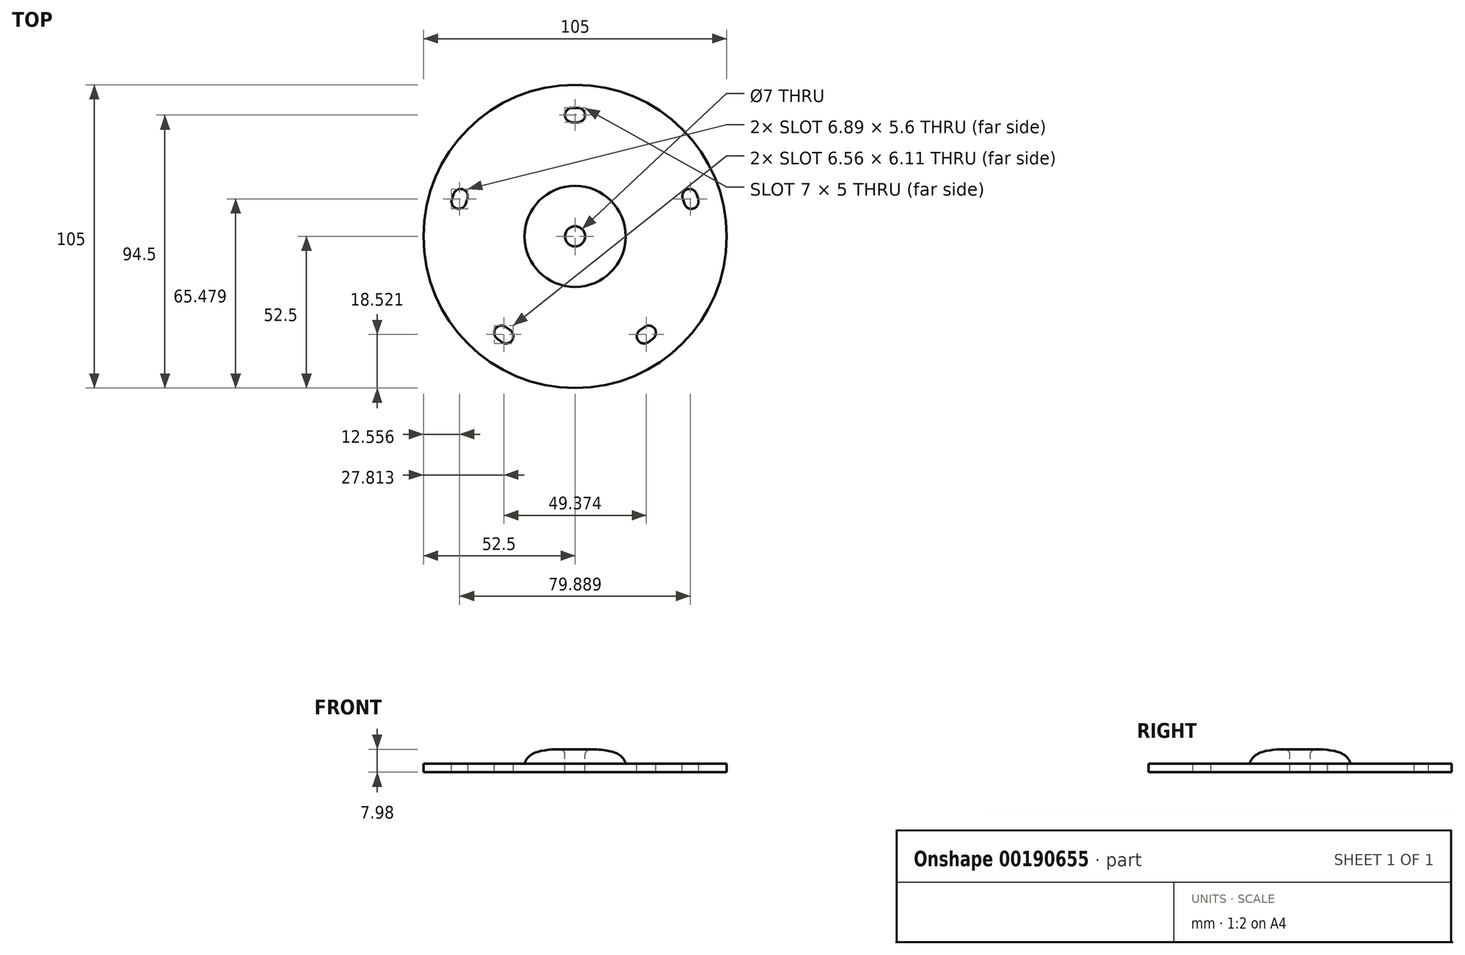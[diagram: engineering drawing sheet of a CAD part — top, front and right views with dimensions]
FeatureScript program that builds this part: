
annotation { "Feature Type Name" : "Feature", "Feature Type Description" : "" }
export const myFeature = defineFeature(function(context is Context, id is Id, definition is map)
    precondition{}
    {
        {
            var Q0;
            Q0=qCreatedBy(makeId("Top.planeOp"),FACE);
            var sketch = newSketch(context, id + "F0", { "sketchPlane" : qUnion([Q0])});
            skCircle(sketch, "E0", {"center": v(0, 0) * mm, "radius": 52.5 * mm});
            skCircle(sketch, "E1", {"center": v(0, 0) * mm, "radius": 42 * mm, "construction": true});
            skLineSegment(sketch, "E2", {"start": v(0, 0) * mm, "end": v(0, 42) * mm, "construction": true});
            skLineSegment(sketch, "E3", {"start": v(-1, 42) * mm, "end": v(1, 42) * mm, "construction": true});
            skArc(sketch, "E4", {"start": v(-1, 44.5) * mm, "mid": v(-3.5, 42) * mm, "end": v(-1, 39.5) * mm});
            skArc(sketch, "E5", {"start": v(1, 39.5) * mm, "mid": v(3.5, 42) * mm, "end": v(1, 44.5) * mm});
            skLineSegment(sketch, "E6", {"start": v(-1, 44.5) * mm, "end": v(1, 44.5) * mm});
            skLineSegment(sketch, "E7", {"start": v(-1, 39.5) * mm, "end": v(1, 39.5) * mm});
            skArc(sketch, "E8.1.0", {"start": v(-42.63, 12.8) * mm, "mid": v(-41.03, 9.65) * mm, "end": v(-37.88, 11.26) * mm});
            skLineSegment(sketch, "E8.1.1", {"start": v(-42.63, 12.8) * mm, "end": v(-42.01, 14.7) * mm});
            skArc(sketch, "E8.1.2", {"start": v(-37.26, 13.16) * mm, "mid": v(-38.86, 16.3) * mm, "end": v(-42.01, 14.7) * mm});
            skLineSegment(sketch, "E8.1.3", {"start": v(-37.88, 11.26) * mm, "end": v(-37.26, 13.16) * mm});
            skArc(sketch, "E8.2.0", {"start": v(-25.35, -36.59) * mm, "mid": v(-21.86, -36.04) * mm, "end": v(-22.4, -32.54) * mm});
            skLineSegment(sketch, "E8.2.1", {"start": v(-25.35, -36.59) * mm, "end": v(-26.97, -35.41) * mm});
            skArc(sketch, "E8.2.2", {"start": v(-24.03, -31.37) * mm, "mid": v(-27.52, -31.92) * mm, "end": v(-26.97, -35.41) * mm});
            skLineSegment(sketch, "E8.2.3", {"start": v(-22.4, -32.54) * mm, "end": v(-24.03, -31.37) * mm});
            skArc(sketch, "E8.3.0", {"start": v(26.97, -35.41) * mm, "mid": v(27.52, -31.92) * mm, "end": v(24.03, -31.37) * mm});
            skLineSegment(sketch, "E8.3.1", {"start": v(26.97, -35.41) * mm, "end": v(25.35, -36.59) * mm});
            skArc(sketch, "E8.3.2", {"start": v(22.4, -32.54) * mm, "mid": v(21.86, -36.04) * mm, "end": v(25.35, -36.59) * mm});
            skLineSegment(sketch, "E8.3.3", {"start": v(24.03, -31.37) * mm, "end": v(22.4, -32.54) * mm});
            skArc(sketch, "E8.4.0", {"start": v(42.01, 14.7) * mm, "mid": v(38.86, 16.3) * mm, "end": v(37.26, 13.16) * mm});
            skLineSegment(sketch, "E8.4.1", {"start": v(42.01, 14.7) * mm, "end": v(42.63, 12.8) * mm});
            skArc(sketch, "E8.4.2", {"start": v(37.88, 11.26) * mm, "mid": v(41.03, 9.65) * mm, "end": v(42.63, 12.8) * mm});
            skLineSegment(sketch, "E8.4.3", {"start": v(37.26, 13.16) * mm, "end": v(37.88, 11.26) * mm});
            skCircle(sketch, "E9", {"center": v(0, 0) * mm, "radius": 17.5 * mm});
            skCircle(sketch, "E10", {"center": v(0, 0) * mm, "radius": 3.5 * mm});
            skSolve(sketch);
        }
        {
            var Q0;
            Q0=makeQuery(id+"F0.imprint","IMPRINT",FACE,{"disambiguationData":[TD([[makeQuery(id+"F0.imprint","IMPRINT",EDGE,{"derivedFrom":sQuery(id+"F0.wireOp",EDGE,"E0")}),1.0]])]});
            var Q1;
            Q1=makeQuery(id+"F0.imprint","IMPRINT",FACE,{"disambiguationData":[TD([[makeQuery(id+"F0.imprint","IMPRINT",EDGE,{"derivedFrom":sQuery(id+"F0.wireOp",EDGE,"E9")}),1.0]])]});
            extrude(context, id + "F1", {"entities" : qUnion([Q0, Q1]), "oppositeDirection" : true, "depth" : 3 * mm});
        }
        {
            var Q0;
            Q0=qCreatedBy(makeId("Front.planeOp"),FACE);
            var sketch = newSketch(context, id + "F2", { "sketchPlane" : qUnion([Q0])});
            skLineSegment(sketch, "E11", {"start": v(0, 0) * mm, "end": v(0, 5) * mm});
            skLineSegment(sketch, "E12.0", {"start": v(-17.5, 0) * mm, "end": v(17.5, 0) * mm});
            skLineSegment(sketch, "E13.bottom", {"start": v(0, 5) * mm, "end": v(17.5, 5) * mm});
            skLineSegment(sketch, "E13.top", {"start": v(0, 0) * mm, "end": v(17.5, 0) * mm});
            skLineSegment(sketch, "E13.left", {"start": v(0, 5) * mm, "end": v(0, 0) * mm});
            skLineSegment(sketch, "E13.right", {"start": v(17.5, 5) * mm, "end": v(17.5, 0) * mm});
            skLineSegment(sketch, "E14", {"start": v(3.5, 0) * mm, "end": v(3.5, 5) * mm});
            skFitSpline(sketch, "E15", {"points": [v(3.5, 5) * mm, v(17.5, 0) * mm], "startDerivative": vector(27.28, 0) * mm, "endDerivative": vector(3.47, -11.27) * mm});
            skSolve(sketch);
        }
        {
            var Q0;
            {var subQ2=sQuery(id+"F2.wireOp",EDGE,"E14");Q0=makeQuery(id+"F2.imprint","IMPRINT",FACE,{"disambiguationData":[TD([[makeQuery(id+"F2.imprint","IMPRINT",EDGE,{"derivedFrom":subQ2}),-1.0]])]});}
            var Q1;
            Q1=sQuery(id+"F2.wireOp",EDGE,"E13.left");
            revolve(context, id + "F3", {"operationType" : NewBodyOperationType.ADD, "entities" : qUnion([Q0]), "axis" : qUnion([Q1]), "revolveType" : RevolveType.FULL});
        }
        {
            var Q0;
            Q0=makeQuery(id+"F3.opRevolve","SWEPT_EDGE",EDGE,{"disambiguationData":[OSD([sQuery(id+"F2.wireOp",EDGE,"E13.bottom"),sQuery(id+"F2.wireOp",EDGE,"E14"),sQuery(id+"F2.wireOp",EDGE,"E15")])]});
            fillet(context, id + "F4", {"entities" : qUnion([Q0]), "radius" : 2 * mm, "tangentPropagation" : true, "allowEdgeOverflow" : false});
        }
    });
